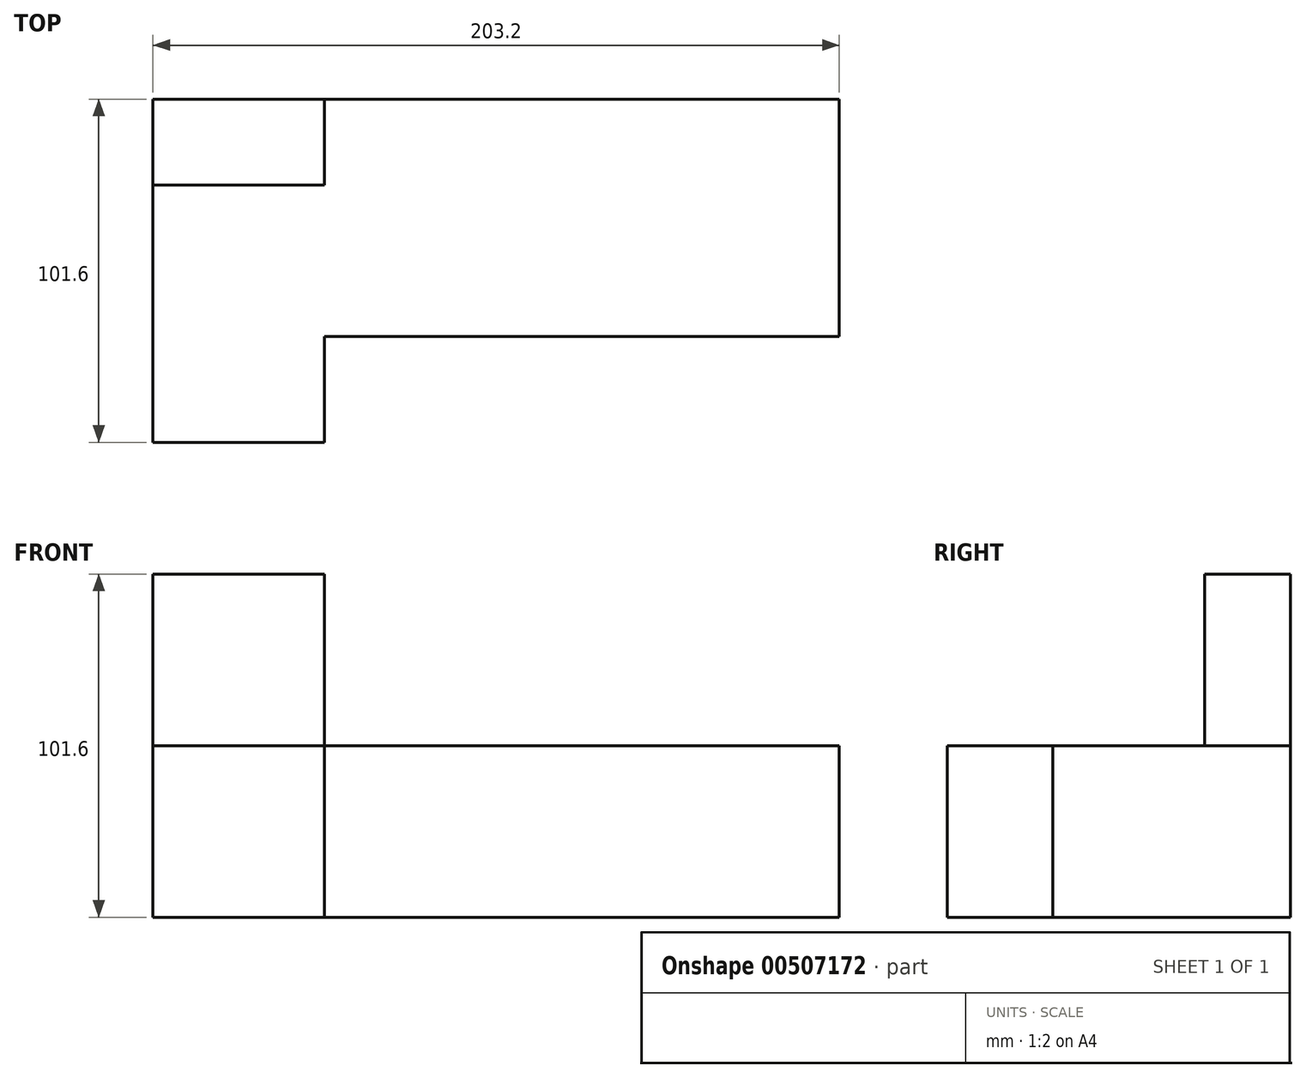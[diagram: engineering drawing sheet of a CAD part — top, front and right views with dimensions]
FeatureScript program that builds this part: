
annotation { "Feature Type Name" : "Feature", "Feature Type Description" : "" }
export const myFeature = defineFeature(function(context is Context, id is Id, definition is map)
    precondition{}
    {
        {
            var Q0;
            Q0=qCreatedBy(makeId("Front.planeOp"),FACE);
            var sketch = newSketch(context, id + "F0", { "sketchPlane" : qUnion([Q0])});
            skLineSegment(sketch, "E0", {"start": v(-76.2, 37.75) * mm, "end": v(0, 37.75) * mm});
            skLineSegment(sketch, "E1", {"start": v(0, 37.75) * mm, "end": v(0, -13.05) * mm});
            skLineSegment(sketch, "E2", {"start": v(0, -13.05) * mm, "end": v(127, -13.05) * mm});
            skLineSegment(sketch, "E3", {"start": v(127, -13.05) * mm, "end": v(127, -63.85) * mm});
            skLineSegment(sketch, "E4", {"start": v(127, -63.85) * mm, "end": v(-76.2, -63.85) * mm});
            skLineSegment(sketch, "E5", {"start": v(-76.2, -63.85) * mm, "end": v(-76.2, 37.75) * mm});
            skSolve(sketch);
        }
        {
            var Q0;
            Q0=qSketchRegion(id+"F0",true);
            extrude(context, id + "F1", {"entities" : qUnion([Q0]), "depth" : 101.6 * mm});
        }
        {
            var Q0;
            Q0=makeQuery(id+"F1.opExtrude","SWEPT_FACE",FACE,{"disambiguationData":[OSD([sQuery(id+"F0.wireOp",EDGE,"E2")])]});
            var sketch = newSketch(context, id + "F2", { "sketchPlane" : qUnion([Q0])});
            skLineSegment(sketch, "E6.bottom", {"start": v(-25.4, 0) * mm, "end": v(0, 0) * mm});
            skLineSegment(sketch, "E6.top", {"start": v(-25.4, -101.6) * mm, "end": v(0, -101.6) * mm});
            skLineSegment(sketch, "E6.left", {"start": v(-25.4, 0) * mm, "end": v(-25.4, -101.6) * mm});
            skLineSegment(sketch, "E6.right", {"start": v(0, 0) * mm, "end": v(0, -101.6) * mm});
            skSolve(sketch);
        }
        {
            var Q0;
            Q0 = qSketchRegion(id + "F2", true);
            extrude(context, id + "F3", {"entities" : qUnion([Q0]), "operationType" : NewBodyOperationType.REMOVE, "depth" : 50.8 * mm});
        }
        {
            var Q0;
            Q0=makeQuery(id+"F3.boolean.opBoolean","MERGE",FACE,{"derivedFrom":[makeQuery(id+"F1.opExtrude","SWEPT_FACE",FACE,{"disambiguationData":[OSD([sQuery(id+"F0.wireOp",EDGE,"E2")])]}),makeQuery(id+"F3.opExtrude","CAP_FACE",FACE,{"disambiguationData":[OSD([sQuery(id+"F2.wireOp",EDGE,"E6.bottom"),sQuery(id+"F2.wireOp",EDGE,"E6.top"),sQuery(id+"F2.wireOp",EDGE,"E6.left"),sQuery(id+"F2.wireOp",EDGE,"E6.right")])],"isStart":true})]});
            var sketch = newSketch(context, id + "F4", { "sketchPlane" : qUnion([Q0])});
            skLineSegment(sketch, "E7.bottom", {"start": v(-25.4, -70.35) * mm, "end": v(127, -70.35) * mm});
            skLineSegment(sketch, "E7.top", {"start": v(-25.4, -101.6) * mm, "end": v(127, -101.6) * mm});
            skLineSegment(sketch, "E7.left", {"start": v(-25.4, -70.35) * mm, "end": v(-25.4, -101.6) * mm});
            skLineSegment(sketch, "E7.right", {"start": v(127, -70.35) * mm, "end": v(127, -101.6) * mm});
            skSolve(sketch);
        }
        {
            var Q0;
            Q0 = qSketchRegion(id + "F4", true);
            extrude(context, id + "F5", {"entities" : qUnion([Q0]), "operationType" : NewBodyOperationType.REMOVE, "oppositeDirection" : true, "depth" : 50.8 * mm});
        }
        {
            var Q0;
            Q0=makeQuery(id+"F1.opExtrude","SWEPT_FACE",FACE,{"disambiguationData":[OSD([sQuery(id+"F0.wireOp",EDGE,"E0")])]});
            var sketch = newSketch(context, id + "F6", { "sketchPlane" : qUnion([Q0])});
            skLineSegment(sketch, "E8.bottom", {"start": v(-76.2, -25.4) * mm, "end": v(-25.4, -25.4) * mm});
            skLineSegment(sketch, "E8.top", {"start": v(-76.2, -101.6) * mm, "end": v(-25.4, -101.6) * mm});
            skLineSegment(sketch, "E8.left", {"start": v(-76.2, -25.4) * mm, "end": v(-76.2, -101.6) * mm});
            skLineSegment(sketch, "E8.right", {"start": v(-25.4, -25.4) * mm, "end": v(-25.4, -101.6) * mm});
            skSolve(sketch);
        }
        {
            var Q0;
            Q0 = qSketchRegion(id + "F6", true);
            extrude(context, id + "F7", {"entities" : qUnion([Q0]), "operationType" : NewBodyOperationType.REMOVE, "oppositeDirection" : true, "depth" : 50.8 * mm});
        }
    });
